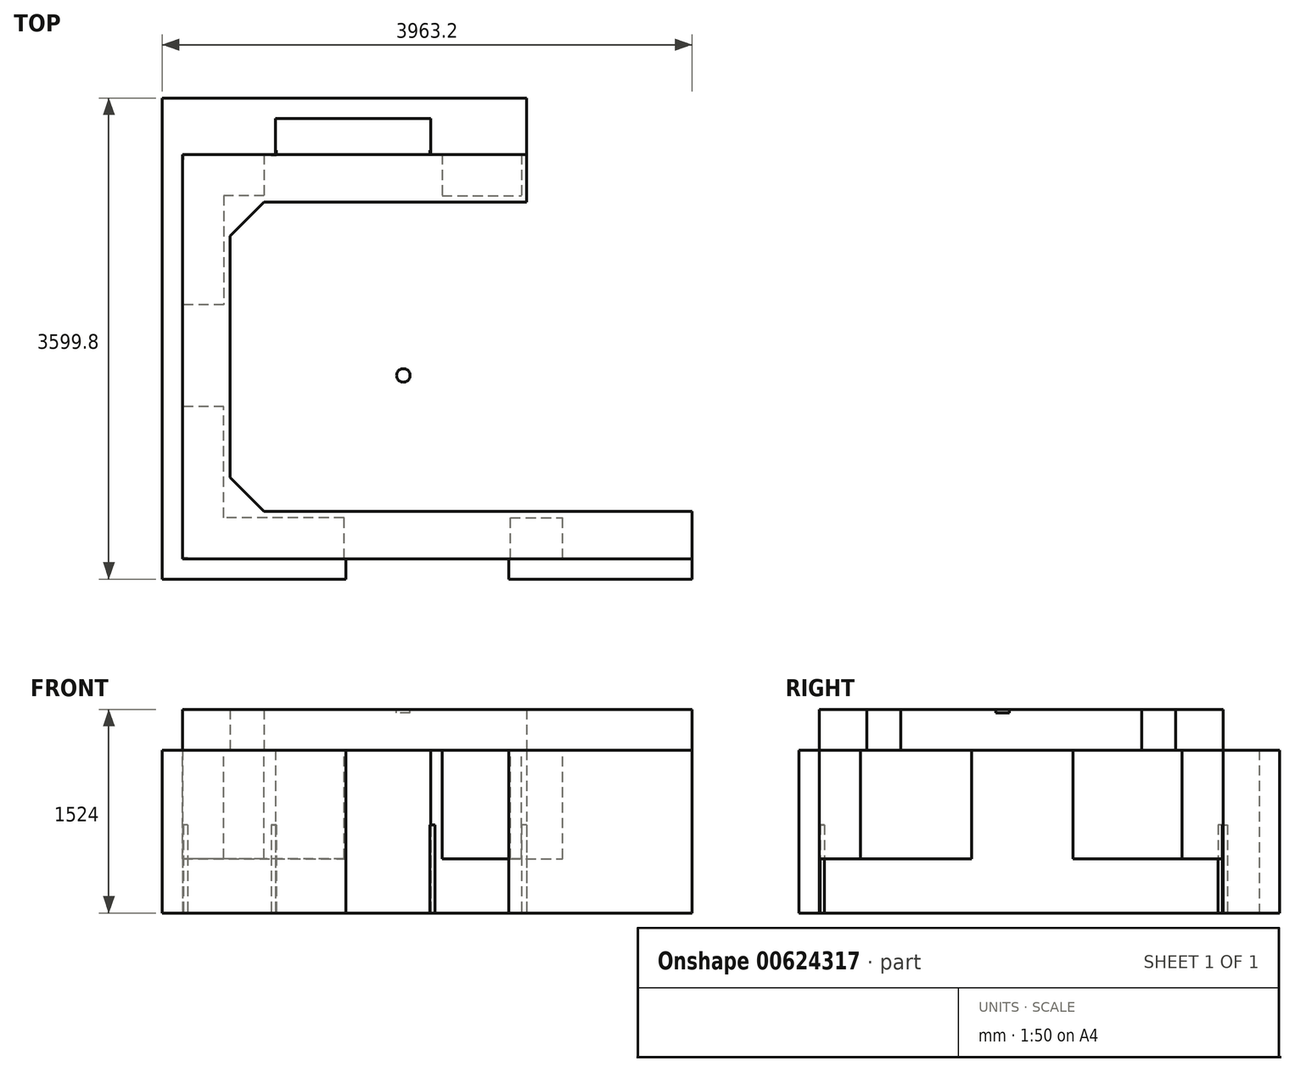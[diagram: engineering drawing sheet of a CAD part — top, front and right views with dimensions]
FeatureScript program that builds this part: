
annotation { "Feature Type Name" : "Feature", "Feature Type Description" : "" }
export const myFeature = defineFeature(function(context is Context, id is Id, definition is map)
    precondition{}
    {
        {
            var Q0;
            Q0=qCreatedBy(makeId("Top.planeOp"),FACE);
            var sketch = newSketch(context, id + "F0", { "sketchPlane" : qUnion([Q0])});
            skLineSegment(sketch, "E0", {"start": v(0, 0) * mm, "end": v(-720, 0) * mm});
            skLineSegment(sketch, "E1", {"start": v(-720, 0) * mm, "end": v(-720, 270) * mm});
            skLineSegment(sketch, "E2", {"start": v(-720, 270) * mm, "end": v(-1880, 270) * mm});
            skLineSegment(sketch, "E3", {"start": v(-1880, 270) * mm, "end": v(-1880, 0) * mm});
            skLineSegment(sketch, "E4", {"start": v(-1880, 0) * mm, "end": v(-2575, 0) * mm});
            skLineSegment(sketch, "E5", {"start": v(-2575, 0) * mm, "end": v(-2575, -3025) * mm});
            skLineSegment(sketch, "E6", {"start": v(-2575, -3025) * mm, "end": v(-1355, -3025) * mm});
            skLineSegment(sketch, "E7", {"start": v(-1355, -3025) * mm, "end": v(-1355, -3177.4) * mm});
            skLineSegment(sketch, "E8", {"start": v(-1355, -3177.4) * mm, "end": v(-2727.4, -3177.4) * mm});
            skLineSegment(sketch, "E9", {"start": v(-2727.4, -3177.4) * mm, "end": v(-2727.4, 422.4) * mm});
            skLineSegment(sketch, "E10", {"start": v(-2727.4, 422.4) * mm, "end": v(0, 422.4) * mm});
            skLineSegment(sketch, "E11", {"start": v(0, 422.4) * mm, "end": v(0, 0) * mm});
            skLineSegment(sketch, "E12.bottom", {"start": v(-135.8, -3025) * mm, "end": v(1235.8, -3025) * mm});
            skLineSegment(sketch, "E12.top", {"start": v(-135.8, -3177.4) * mm, "end": v(1235.8, -3177.4) * mm});
            skLineSegment(sketch, "E12.left", {"start": v(-135.8, -3025) * mm, "end": v(-135.8, -3177.4) * mm});
            skLineSegment(sketch, "E12.right", {"start": v(1235.8, -3025) * mm, "end": v(1235.8, -3177.4) * mm});
            skSolve(sketch);
        }
        {
            var Q0;
            Q0 = qSketchRegion(id + "F0", true);
            extrude(context, id + "F1", {"entities" : qUnion([Q0]), "depth" : 1219.2 * mm, "offsetDistance" : 25.4 * mm});
        }
        {
            var Q0;
            Q0=makeQuery(id+"F1.opExtrude","CAP_FACE",FACE,{"disambiguationData":[OSD([sQuery(id+"F0.wireOp",EDGE,"E0"),sQuery(id+"F0.wireOp",EDGE,"E1"),sQuery(id+"F0.wireOp",EDGE,"E2"),sQuery(id+"F0.wireOp",EDGE,"E3"),sQuery(id+"F0.wireOp",EDGE,"E4"),sQuery(id+"F0.wireOp",EDGE,"E5"),sQuery(id+"F0.wireOp",EDGE,"E6"),sQuery(id+"F0.wireOp",EDGE,"E7"),sQuery(id+"F0.wireOp",EDGE,"E8"),sQuery(id+"F0.wireOp",EDGE,"E9"),sQuery(id+"F0.wireOp",EDGE,"E10"),sQuery(id+"F0.wireOp",EDGE,"E11")])],"isStart":false});
            var sketch = newSketch(context, id + "F2", { "sketchPlane" : qUnion([Q0])});
            skLineSegment(sketch, "E13.bottom", {"start": v(-634.27, 0) * mm, "end": v(-38.1, 0) * mm});
            skLineSegment(sketch, "E13.top", {"start": v(-634.27, -307.98) * mm, "end": v(-38.1, -307.97) * mm});
            skLineSegment(sketch, "E13.left", {"start": v(-634.27, 0) * mm, "end": v(-634.27, -307.98) * mm});
            skLineSegment(sketch, "E13.right", {"start": v(-38.1, 0) * mm, "end": v(-38.1, -307.97) * mm});
            skLineSegment(sketch, "E14", {"start": v(-1965.72, 0) * mm, "end": v(-1965.72, -307.98) * mm});
            skLineSegment(sketch, "E15", {"start": v(-1965.72, -307.98) * mm, "end": v(-2267.03, -307.98) * mm});
            skLineSegment(sketch, "E16", {"start": v(-2267.03, -307.98) * mm, "end": v(-2267.03, -1123.95) * mm});
            skLineSegment(sketch, "E17", {"start": v(-2267.03, -1123.95) * mm, "end": v(-2575, -1123.95) * mm});
            skLineSegment(sketch, "E18", {"start": v(-1965.72, 0) * mm, "end": v(-2575, 0) * mm});
            skLineSegment(sketch, "E19", {"start": v(-2575, 0) * mm, "end": v(-2575, -1123.95) * mm});
            skLineSegment(sketch, "E20", {"start": v(-2575, -1885.17) * mm, "end": v(-2575, -3025) * mm});
            skLineSegment(sketch, "E21", {"start": v(-2575, -3025) * mm, "end": v(-1367.7, -3025) * mm});
            skLineSegment(sketch, "E22", {"start": v(-1367.7, -3025) * mm, "end": v(-1367.7, -2717.02) * mm});
            skLineSegment(sketch, "E23", {"start": v(-1367.7, -2717.03) * mm, "end": v(-2267.03, -2717.03) * mm});
            skLineSegment(sketch, "E24", {"start": v(-2267.03, -2717.03) * mm, "end": v(-2267.03, -1885.17) * mm});
            skLineSegment(sketch, "E25", {"start": v(-2267.03, -1885.17) * mm, "end": v(-2575, -1885.17) * mm});
            skLineSegment(sketch, "E26.bottom", {"start": v(-123.1, -3025) * mm, "end": v(267.43, -3025) * mm});
            skLineSegment(sketch, "E26.top", {"start": v(-123.1, -2717.02) * mm, "end": v(267.43, -2717.02) * mm});
            skLineSegment(sketch, "E26.left", {"start": v(-123.1, -3025) * mm, "end": v(-123.1, -2717.02) * mm});
            skLineSegment(sketch, "E26.right", {"start": v(267.43, -3025) * mm, "end": v(267.43, -2717.02) * mm});
            skSolve(sketch);
        }
        {
            var Q0;
            Q0 = qSketchRegion(id + "F2", true);
            extrude(context, id + "F3", {"entities" : qUnion([Q0]), "oppositeDirection" : true, "depth" : 812.8 * mm, "offsetDistance" : 25.4 * mm});
        }
        {
            var Q0;
            Q0=makeQuery(id+"F1.opExtrude","CAP_FACE",FACE,{"disambiguationData":[OSD([sQuery(id+"F0.wireOp",EDGE,"E0"),sQuery(id+"F0.wireOp",EDGE,"E1"),sQuery(id+"F0.wireOp",EDGE,"E2"),sQuery(id+"F0.wireOp",EDGE,"E3"),sQuery(id+"F0.wireOp",EDGE,"E4"),sQuery(id+"F0.wireOp",EDGE,"E5"),sQuery(id+"F0.wireOp",EDGE,"E6"),sQuery(id+"F0.wireOp",EDGE,"E7"),sQuery(id+"F0.wireOp",EDGE,"E8"),sQuery(id+"F0.wireOp",EDGE,"E9"),sQuery(id+"F0.wireOp",EDGE,"E10"),sQuery(id+"F0.wireOp",EDGE,"E11")])],"isStart":true});
            var sketch = newSketch(context, id + "F4", { "sketchPlane" : qUnion([Q0])});
            skLineSegment(sketch, "E27.bottom", {"start": v(0, 0) * mm, "end": v(-38.1, 0) * mm});
            skLineSegment(sketch, "E27.top", {"start": v(0, 6.35) * mm, "end": v(-38.1, 6.35) * mm});
            skLineSegment(sketch, "E27.left", {"start": v(0, 0) * mm, "end": v(0, 6.35) * mm});
            skLineSegment(sketch, "E27.right", {"start": v(-38.1, 0) * mm, "end": v(-38.1, 6.35) * mm});
            skLineSegment(sketch, "E28", {"start": v(-688.25, 0) * mm, "end": v(-688.25, 6.35) * mm});
            skLineSegment(sketch, "E29", {"start": v(-688.25, 6.35) * mm, "end": v(-726.35, 6.35) * mm});
            skLineSegment(sketch, "E30", {"start": v(-726.35, 6.35) * mm, "end": v(-726.35, -31.75) * mm});
            skLineSegment(sketch, "E31", {"start": v(-726.35, -31.75) * mm, "end": v(-720, -31.75) * mm});
            skLineSegment(sketch, "E32", {"start": v(-720, -31.75) * mm, "end": v(-720, 0) * mm});
            skLineSegment(sketch, "E33", {"start": v(-720, 0) * mm, "end": v(-688.25, 0) * mm});
            skLineSegment(sketch, "E34", {"start": v(-1911.75, 0) * mm, "end": v(-1911.75, 6.35) * mm});
            skLineSegment(sketch, "E35", {"start": v(-1911.75, 6.35) * mm, "end": v(-1873.65, 6.35) * mm});
            skLineSegment(sketch, "E36", {"start": v(-1873.65, 6.35) * mm, "end": v(-1873.65, -31.75) * mm});
            skLineSegment(sketch, "E37", {"start": v(-1873.65, -31.75) * mm, "end": v(-1880, -31.75) * mm});
            skLineSegment(sketch, "E38", {"start": v(-1880, -31.75) * mm, "end": v(-1880, 0) * mm});
            skLineSegment(sketch, "E39", {"start": v(-1880, 0) * mm, "end": v(-1911.75, 0) * mm});
            skLineSegment(sketch, "E40", {"start": v(-2575, 0) * mm, "end": v(-2536.9, 0) * mm});
            skLineSegment(sketch, "E41", {"start": v(-2536.9, 0) * mm, "end": v(-2536.9, 6.35) * mm});
            skLineSegment(sketch, "E42", {"start": v(-2536.9, 6.35) * mm, "end": v(-2568.65, 6.35) * mm});
            skLineSegment(sketch, "E43", {"start": v(-2568.65, 6.35) * mm, "end": v(-2568.65, 38.1) * mm});
            skLineSegment(sketch, "E44", {"start": v(-2568.65, 38.1) * mm, "end": v(-2575, 38.1) * mm});
            skLineSegment(sketch, "E45", {"start": v(-2575, 38.1) * mm, "end": v(-2575, 0) * mm});
            skLineSegment(sketch, "E46", {"start": v(-2575, 3025) * mm, "end": v(-2536.9, 3025) * mm});
            skLineSegment(sketch, "E47", {"start": v(-2536.9, 3025) * mm, "end": v(-2536.9, 3018.65) * mm});
            skLineSegment(sketch, "E48", {"start": v(-2536.9, 3018.65) * mm, "end": v(-2568.65, 3018.65) * mm});
            skLineSegment(sketch, "E49", {"start": v(-2568.65, 3018.65) * mm, "end": v(-2568.65, 2986.9) * mm});
            skLineSegment(sketch, "E50", {"start": v(-2568.65, 2986.9) * mm, "end": v(-2575, 2986.9) * mm});
            skLineSegment(sketch, "E51", {"start": v(-2575, 2986.9) * mm, "end": v(-2575, 3025) * mm});
            skSolve(sketch);
        }
        {
            var Q0;
            Q0 = qSketchRegion(id + "F4", true);
            var Q1;
            Q1=makeQuery(id+"F3.opExtrude","CAP_FACE",FACE,{"disambiguationData":[OSD([sQuery(id+"F2.wireOp",EDGE,"E20"),sQuery(id+"F2.wireOp",EDGE,"E21"),sQuery(id+"F2.wireOp",EDGE,"E22"),sQuery(id+"F2.wireOp",EDGE,"E23"),sQuery(id+"F2.wireOp",EDGE,"E24"),sQuery(id+"F2.wireOp",EDGE,"E25")])],"isStart":false});
            extrude(context, id + "F5", {"entities" : qUnion([Q0]), "oppositeDirection" : true, "depth" : 660.4 * mm, "endBoundEntityFace" : qUnion([Q1]), "offsetDistance" : 25.4 * mm});
        }
        {
            var Q0;
            Q0=makeQuery(id+"F1.opExtrude","CAP_FACE",FACE,{"disambiguationData":[OSD([sQuery(id+"F0.wireOp",EDGE,"E0"),sQuery(id+"F0.wireOp",EDGE,"E1"),sQuery(id+"F0.wireOp",EDGE,"E2"),sQuery(id+"F0.wireOp",EDGE,"E3"),sQuery(id+"F0.wireOp",EDGE,"E4"),sQuery(id+"F0.wireOp",EDGE,"E5"),sQuery(id+"F0.wireOp",EDGE,"E6"),sQuery(id+"F0.wireOp",EDGE,"E7"),sQuery(id+"F0.wireOp",EDGE,"E8"),sQuery(id+"F0.wireOp",EDGE,"E9"),sQuery(id+"F0.wireOp",EDGE,"E10"),sQuery(id+"F0.wireOp",EDGE,"E11")])],"isStart":false});
            var sketch = newSketch(context, id + "F6", { "sketchPlane" : qUnion([Q0])});
            skLineSegment(sketch, "E52", {"start": v(-2575, -3025) * mm, "end": v(1235.8, -3025) * mm});
            skLineSegment(sketch, "E53", {"start": v(1235.8, -3025) * mm, "end": v(1235.8, -2669.4) * mm});
            skLineSegment(sketch, "E54", {"start": v(1235.8, -2669.4) * mm, "end": v(-1965.4, -2669.4) * mm});
            skLineSegment(sketch, "E55", {"start": v(-1965.4, -2669.4) * mm, "end": v(-2219.4, -2415.4) * mm});
            skLineSegment(sketch, "E56", {"start": v(-2219.4, -2415.4) * mm, "end": v(-2219.4, -609.6) * mm});
            skLineSegment(sketch, "E57", {"start": v(-2219.4, -609.6) * mm, "end": v(-1965.4, -355.6) * mm});
            skLineSegment(sketch, "E58", {"start": v(-1965.4, -355.6) * mm, "end": v(0, -355.6) * mm});
            skLineSegment(sketch, "E59", {"start": v(0, -355.6) * mm, "end": v(0, 0) * mm});
            skLineSegment(sketch, "E60", {"start": v(0, 0) * mm, "end": v(-2575, 0) * mm});
            skLineSegment(sketch, "E61", {"start": v(-2575, 0) * mm, "end": v(-2575, -3025) * mm});
            skSolve(sketch);
        }
        {
            var Q0;
            Q0 = qSketchRegion(id + "F6", true);
            extrude(context, id + "F7", {"entities" : qUnion([Q0]), "depth" : 304.8 * mm, "offsetDistance" : 25.4 * mm});
        }
        {
            var Q0;
            Q0=makeQuery(id+"F7.opExtrude","CAP_FACE",FACE,{"disambiguationData":[OSD([sQuery(id+"F6.wireOp",EDGE,"E52"),sQuery(id+"F6.wireOp",EDGE,"E53"),sQuery(id+"F6.wireOp",EDGE,"E54"),sQuery(id+"F6.wireOp",EDGE,"E55"),sQuery(id+"F6.wireOp",EDGE,"E56"),sQuery(id+"F6.wireOp",EDGE,"E57"),sQuery(id+"F6.wireOp",EDGE,"E58"),sQuery(id+"F6.wireOp",EDGE,"E59"),sQuery(id+"F6.wireOp",EDGE,"E60"),sQuery(id+"F6.wireOp",EDGE,"E61")])],"isStart":false});
            var sketch = newSketch(context, id + "F8", { "sketchPlane" : qUnion([Q0])});
            skCircle(sketch, "E62", {"center": v(-924, -1653.4) * mm, "radius": 50.8 * mm});
            skLineSegment(sketch, "E63", {"start": v(-924, -1653.4) * mm, "end": v(-2219.4, -1653.4) * mm, "construction": true});
            skLineSegment(sketch, "E64", {"start": v(-924, -1653.4) * mm, "end": v(-924, -2669.4) * mm, "construction": true});
            skSolve(sketch);
        }
        {
            var Q0;
            Q0 = qSketchRegion(id + "F8", true);
            extrude(context, id + "F9", {"entities" : qUnion([Q0]), "oppositeDirection" : true, "depth" : 25.4 * mm, "offsetDistance" : 25.4 * mm});
        }
    });
